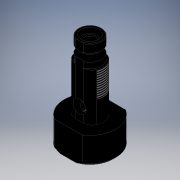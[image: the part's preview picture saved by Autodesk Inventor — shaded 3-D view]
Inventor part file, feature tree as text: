
AUTODESK INVENTOR PART (.ipt)
format: ipt  version: 2019 (Build 230136000, 136)  size: 220,672 bytes
history: native  units: mm
features: other x7, extrude x3, hole x3, chamfer x2, sketch x1
ambient origin geometry x8: Origin, YZ Plane, XZ Plane, XY Plane, X Axis, Y Axis, Z Axis, Center Point
bodies: Solid1 (feature_tree)
feature tree (16):
  extrude  "Spigot Base"  Depth=9.5mm
  extrude  "Spigot"  Depth=9.5mm
  other  "Spigot Axis"
  other  "Clip Cutout"
  hole  "Connector Hole"  [1 undecoded]
  extrude  "Orientation Cutout"  Depth=10.0mm
  hole  "Cable Hole"  [1 undecoded]
  chamfer  "Top Chamfer"  Distance=9.9mm
  chamfer  "Bottom Chamfer"  Distance=25.5mm
  hole  "Box Fastening Hole"  [1 undecoded]
  other  "Spigot Base Outline"
  other  "Spigot Cross Section"
  other  "Clip Cutout Profile"
  other  "Orientation Cutout Profile"
  other  "Cable Hole Position"
  sketch  "Sketch9"  dims[d0=19.0mm d1=9.5mm d2=9.5mm d3=8.0mm d4=8.0mm d5=10.0mm d6=0.0mm d7=9.9mm d8=25.5mm d9=0.0mm d10=45.0deg d11=45.0deg d12=2.5mm d13=0.0mm d15=8.0mm d16=3.457005mm d17=4.6mm d18=4.5mm d19=4.25mm d20=90.0deg d21=9.5mm d22=0.0mm d58=10.0mm d59=10.0mm d25=4.826mm d26=6.0mm d27=6.477mm d28=2.032mm d29=90.0deg d30=25.0mm d31=20.594885mm d38=4.95mm d39=3.95mm d40=3.25mm d41=20.0mm d42=10.0mm d43=20.0mm d44=10.0mm d45=25.5mm d46=0.0mm d47=0.0mm d48=21.0mm d49=4.826mm d50=6.0mm d51=6.477mm d52=2.032mm d53=90.0deg d54=4.0mm d55=0.0mm d61=0.254mm d62=2.0mm d63=45.0deg d64=1.0mm d65=2.0mm d66=45.0deg d67=10.0mm d68=10.0mm d69=4.134mm d70=10.0mm d71=4.0mm d72=2.0mm d73=90.0deg d74=14.2mm d75=20.594885mm]
note: 3 required parameter values undecoded (feature->parameter linkage not recoverable at this tier; creation-order binding heuristic only, values carry confidence <= 0.55)
